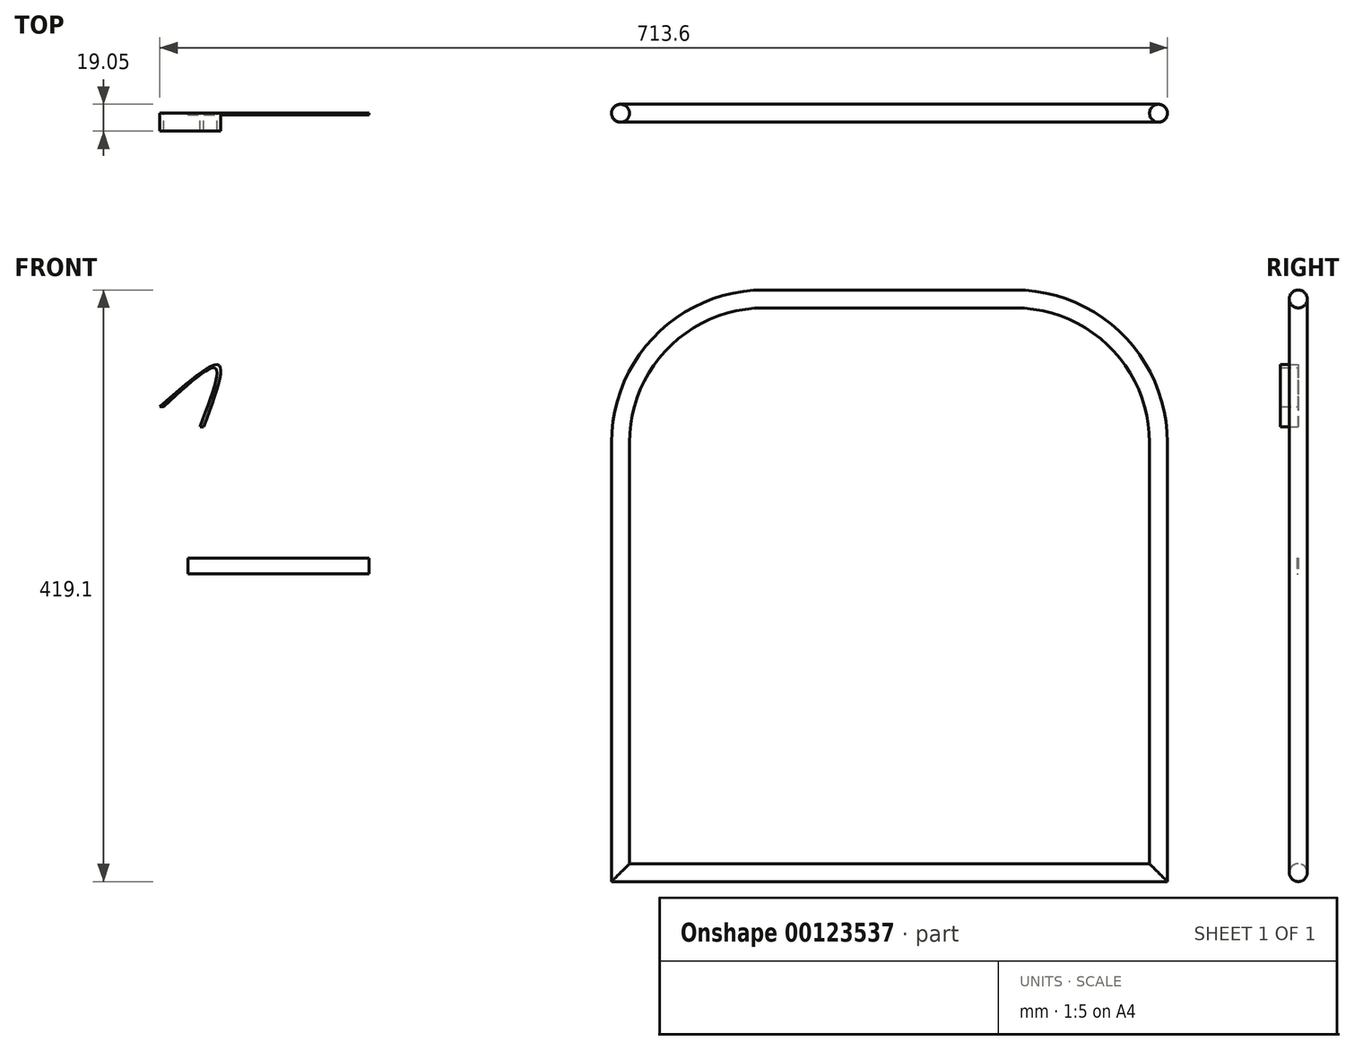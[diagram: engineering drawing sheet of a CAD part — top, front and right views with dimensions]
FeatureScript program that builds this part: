
annotation { "Feature Type Name" : "Feature", "Feature Type Description" : "" }
export const myFeature = defineFeature(function(context is Context, id is Id, definition is map)
    precondition{}
    {
        {
            var Q0;
            Q0=qCreatedBy(makeId("Front.planeOp"),FACE);
            var sketch = newSketch(context, id + "F0", { "sketchPlane" : qUnion([Q0])});
            skLineSegment(sketch, "E0", {"start": v(0, 0) * mm, "end": v(0, 304.8) * mm});
            skLineSegment(sketch, "E1", {"start": v(101.6, 406.4) * mm, "end": v(279.4, 406.4) * mm});
            skLineSegment(sketch, "E2", {"start": v(381, 304.8) * mm, "end": v(381, 0) * mm});
            skLineSegment(sketch, "E3", {"start": v(381, 0) * mm, "end": v(0, 0) * mm});
            skPoint(sketch, "E4.visualSharp", {"position": v(0, 406.4) * mm});
            skArc(sketch, "E4.filletArc", {"start": v(101.6, 406.4) * mm, "mid": v(29.76, 376.64) * mm, "end": v(0, 304.8) * mm});
            skPoint(sketch, "E5.visualSharp", {"position": v(381, 406.4) * mm});
            skArc(sketch, "E5.filletArc", {"start": v(381, 304.8) * mm, "mid": v(351.24, 376.64) * mm, "end": v(279.4, 406.4) * mm});
            skSolve(sketch);
        }
        {
            var Q0;
            Q0=qCreatedBy(makeId("Right.planeOp"),FACE);
            var sketch = newSketch(context, id + "F1", { "sketchPlane" : qUnion([Q0])});
            skCircle(sketch, "E6", {"center": v(0, 0) * mm, "radius": 6.35 * mm});
            skSolve(sketch);
        }
        {
            var Q0;
            Q0=makeQuery(id+"F1.imprint","IMPRINT",FACE,{"disambiguationData":[TD([[makeQuery(id+"F1.imprint","IMPRINT",EDGE,{"derivedFrom":sQuery(id+"F1.wireOp",EDGE,"E6")}),1.0]])]});
            var Q1;
            Q1=sQuery(id+"F0.wireOp",EDGE,"E0");
            var Q2;
            Q2=sQuery(id+"F0.wireOp",EDGE,"E4.filletArc");
            var Q3;
            Q3=sQuery(id+"F0.wireOp",EDGE,"E1");
            var Q4;
            Q4=sQuery(id+"F0.wireOp",EDGE,"E5.filletArc");
            var Q5;
            Q5=sQuery(id+"F0.wireOp",EDGE,"E2");
            var Q6;
            Q6=sQuery(id+"F0.wireOp",EDGE,"E3");
            sweep(context, id + "F2", {"profiles" : qUnion([Q0]), "path" : qUnion([Q1, Q2, Q3, Q4, Q5, Q6])});
        }
        {
            var Q0;
            Q0=qCreatedBy(makeId("Front.planeOp"),FACE);
            var sketch = newSketch(context, id + "F3", { "sketchPlane" : qUnion([Q0])});
            skLineSegment(sketch, "E7.bottom", {"start": v(-306.45, 222.76) * mm, "end": v(-178, 222.76) * mm});
            skLineSegment(sketch, "E7.top", {"start": v(-306.45, 211.8) * mm, "end": v(-178, 211.8) * mm});
            skLineSegment(sketch, "E7.left", {"start": v(-306.45, 222.76) * mm, "end": v(-306.45, 211.8) * mm});
            skLineSegment(sketch, "E7.right", {"start": v(-178, 222.76) * mm, "end": v(-178, 211.8) * mm});
            skSolve(sketch);
        }
        {
            var Q0;
            Q0 = qSketchRegion(id + "F3", true);
            extrude(context, id + "F4", {"entities" : qUnion([Q0]), "depth" : 1.02 * mm});
        }
        {
            var Q0;
            Q0=qCreatedBy(makeId("Front.planeOp"),FACE);
            var sketch = newSketch(context, id + "F5", { "sketchPlane" : qUnion([Q0])});
            skFitSpline(sketch, "E8", {"points": [v(-323.68, 330.07) * mm, v(-286.87, 357.49) * mm, v(-297.83, 315.97) * mm], "startDerivative": vector(96.5, 89.1) * mm, "endDerivative": vector(-45.6, -118.45) * mm});
            skLineSegment(sketch, "E9", {"start": v(-297.83, 315.97) * mm, "end": v(-295.16, 315.97) * mm});
            skLineSegment(sketch, "E10", {"start": v(-323.68, 330.07) * mm, "end": v(-326.25, 330.07) * mm});
            skLineSegment(sketch, "E11", {"start": v(-326.25, 330.07) * mm, "end": v(-326.25, 332.21) * mm});
            skFitSpline(sketch, "E12", {"points": [v(-295.16, 315.97) * mm, v(-284.45, 359.54) * mm, v(-326.25, 330.07) * mm], "startDerivative": vector(47.07, 125.66) * mm, "endDerivative": vector(-107.55, -95.06) * mm});
            skSolve(sketch);
        }
        {
            var Q0;
            Q0 = qSketchRegion(id + "F5", true);
            extrude(context, id + "F6", {"entities" : qUnion([Q0]), "depth" : 12.7 * mm});
        }
    });
